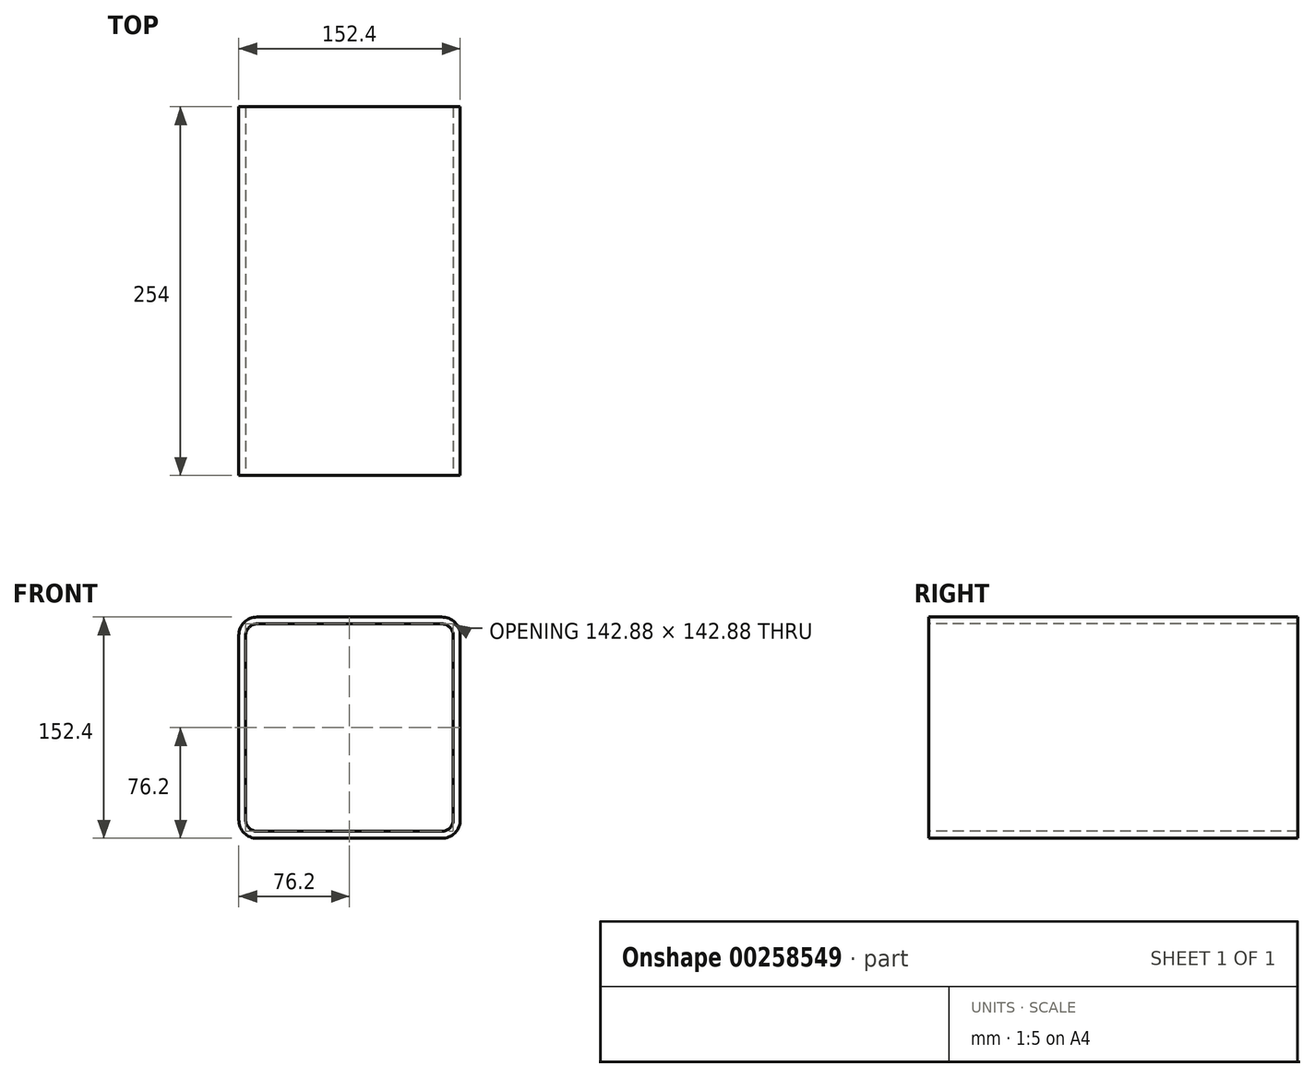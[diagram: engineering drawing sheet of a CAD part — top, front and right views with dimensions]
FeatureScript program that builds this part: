
annotation { "Feature Type Name" : "Feature", "Feature Type Description" : "" }
export const myFeature = defineFeature(function(context is Context, id is Id, definition is map)
    precondition{}
    {
        {
            var Q0;
            Q0=qCreatedBy(makeId("Front.planeOp"),FACE);
            var sketch = newSketch(context, id + "F0", { "sketchPlane" : qUnion([Q0])});
            skLineSegment(sketch, "E0.bottom", {"start": v(-63.5, -76.2) * mm, "end": v(63.5, -76.2) * mm});
            skLineSegment(sketch, "E0.top", {"start": v(-63.5, 76.2) * mm, "end": v(63.5, 76.2) * mm});
            skLineSegment(sketch, "E0.left", {"start": v(-76.2, -63.5) * mm, "end": v(-76.2, 63.5) * mm});
            skLineSegment(sketch, "E0.right", {"start": v(76.2, -63.5) * mm, "end": v(76.2, 63.5) * mm});
            skPoint(sketch, "E0.middle", {"position": v(0, 0) * mm});
            skPoint(sketch, "E1.visualSharp", {"position": v(76.2, 76.2) * mm});
            skArc(sketch, "E1.filletArc", {"start": v(76.2, 63.5) * mm, "mid": v(72.48, 72.48) * mm, "end": v(63.5, 76.2) * mm});
            skArc(sketch, "E2.filletArc", {"start": v(-63.5, 76.2) * mm, "mid": v(-72.48, 72.48) * mm, "end": v(-76.2, 63.5) * mm});
            skPoint(sketch, "E3.visualSharp", {"position": v(-76.2, -76.2) * mm});
            skArc(sketch, "E3.filletArc", {"start": v(-76.2, -63.5) * mm, "mid": v(-72.48, -72.48) * mm, "end": v(-63.5, -76.2) * mm});
            skPoint(sketch, "E4.visualSharp", {"position": v(76.2, -76.2) * mm});
            skArc(sketch, "E4.filletArc", {"start": v(63.5, -76.2) * mm, "mid": v(72.48, -72.48) * mm, "end": v(76.2, -63.5) * mm});
            skArc(sketch, "E5.0", {"start": v(-63.5, 71.44) * mm, "mid": v(-69.11, 69.11) * mm, "end": v(-71.44, 63.5) * mm});
            skLineSegment(sketch, "E5.1", {"start": v(-71.44, -63.5) * mm, "end": v(-71.44, 63.5) * mm});
            skLineSegment(sketch, "E5.2", {"start": v(-63.5, 71.44) * mm, "end": v(63.5, 71.44) * mm});
            skArc(sketch, "E5.3", {"start": v(-71.44, -63.5) * mm, "mid": v(-69.11, -69.11) * mm, "end": v(-63.5, -71.44) * mm});
            skArc(sketch, "E5.4", {"start": v(71.44, 63.5) * mm, "mid": v(69.11, 69.11) * mm, "end": v(63.5, 71.44) * mm});
            skLineSegment(sketch, "E5.5", {"start": v(71.44, -63.5) * mm, "end": v(71.44, 63.5) * mm});
            skArc(sketch, "E5.6", {"start": v(63.5, -71.44) * mm, "mid": v(69.11, -69.11) * mm, "end": v(71.44, -63.5) * mm});
            skLineSegment(sketch, "E5.7", {"start": v(-63.5, -71.44) * mm, "end": v(63.5, -71.44) * mm});
            skSolve(sketch);
        }
        {
            var Q0;
            Q0=makeQuery(id+"F0.imprint","IMPRINT",FACE,{"disambiguationData":[TD([[makeQuery(id+"F0.imprint","IMPRINT",EDGE,{"derivedFrom":sQuery(id+"F0.wireOp",EDGE,"E0.bottom")}),1.0]])]});
            extrude(context, id + "F1", {"entities" : qUnion([Q0]), "oppositeDirection" : true, "depth" : 254 * mm});
        }
    });
